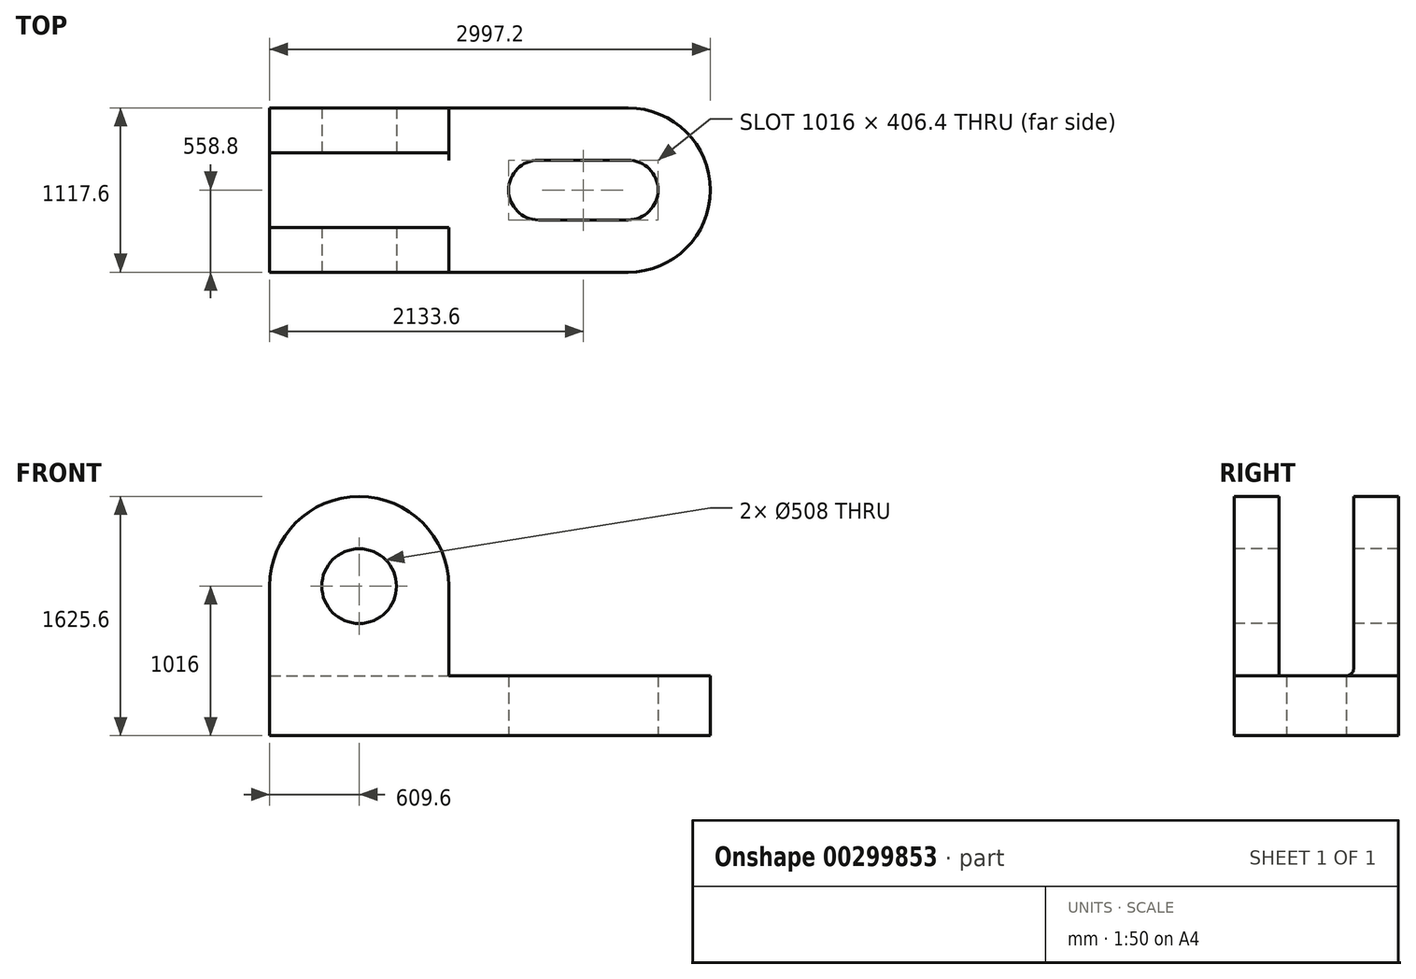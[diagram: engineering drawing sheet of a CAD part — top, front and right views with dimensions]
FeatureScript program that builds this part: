
annotation { "Feature Type Name" : "Feature", "Feature Type Description" : "" }
export const myFeature = defineFeature(function(context is Context, id is Id, definition is map)
    precondition{}
    {
        {
            var Q0;
            Q0=qCreatedBy(makeId("Top.planeOp"),FACE);
            var sketch = newSketch(context, id + "F0", { "sketchPlane" : qUnion([Q0])});
            skLineSegment(sketch, "E0", {"start": v(0, -558.8) * mm, "end": v(2438.4, -558.8) * mm});
            skArc(sketch, "E1", {"start": v(2438.4, -558.8) * mm, "mid": v(2997.2, 0) * mm, "end": v(2438.4, 558.8) * mm});
            skLineSegment(sketch, "E2", {"start": v(0, -558.8) * mm, "end": v(0, 558.8) * mm});
            skLineSegment(sketch, "E3", {"start": v(0, 558.8) * mm, "end": v(2438.4, 558.8) * mm});
            skArc(sketch, "E4", {"start": v(2438.4, 203.2) * mm, "mid": v(2641.6, 0) * mm, "end": v(2438.4, -203.2) * mm});
            skLineSegment(sketch, "E5", {"start": v(2438.4, 203.2) * mm, "end": v(1828.8, 203.2) * mm});
            skArc(sketch, "E6", {"start": v(1828.8, 203.2) * mm, "mid": v(1625.6, 0) * mm, "end": v(1828.8, -203.2) * mm});
            skLineSegment(sketch, "E7", {"start": v(1828.8, -203.2) * mm, "end": v(2438.4, -203.2) * mm});
            skSolve(sketch);
        }
        {
            var Q0;
            Q0 = qSketchRegion(id + "F0", true);
            extrude(context, id + "F1", {"entities" : qUnion([Q0]), "depth" : 406.4 * mm});
        }
        {
            var Q0;
            Q0=makeQuery(id+"F1.opExtrude","SWEPT_FACE",FACE,{"disambiguationData":[OSD([sQuery(id+"F0.wireOp",EDGE,"E0")])]});
            var sketch = newSketch(context, id + "F2", { "sketchPlane" : qUnion([Q0])});
            skPoint(sketch, "E8", {"position": v(609.6, 1016) * mm});
            skCircle(sketch, "E9", {"center": v(609.6, 1016) * mm, "radius": 254 * mm});
            skArc(sketch, "E10", {"start": v(0, 1016) * mm, "mid": v(609.6, 1625.6) * mm, "end": v(1219.2, 1016) * mm});
            skLineSegment(sketch, "E11", {"start": v(0, 1016) * mm, "end": v(0, 406.4) * mm});
            skLineSegment(sketch, "E12", {"start": v(1219.2, 1016) * mm, "end": v(1219.2, 406.4) * mm});
            skLineSegment(sketch, "E13", {"start": v(1219.2, 406.4) * mm, "end": v(0, 406.4) * mm});
            skSolve(sketch);
        }
        {
            var Q0;
            Q0 = qSketchRegion(id + "F2", true);
            extrude(context, id + "F3", {"entities" : qUnion([Q0]), "operationType" : NewBodyOperationType.ADD, "oppositeDirection" : true, "depth" : 1117.6 * mm});
        }
        {
            var Q0;
            Q0 = qSketchRegion(id + "F2", true);
            extrude(context, id + "F4", {"entities" : qUnion([Q0]), "operationType" : NewBodyOperationType.REMOVE, "oppositeDirection" : true, "depth" : 812.8 * mm});
        }
        {
            var Q0;
            Q0 = qSketchRegion(id + "F2", true);
            extrude(context, id + "F5", {"entities" : qUnion([Q0]), "operationType" : NewBodyOperationType.ADD, "oppositeDirection" : true, "depth" : 304.8 * mm});
        }
        {
            var Q0;
            Q0=makeQuery(id+"F5.opExtrude","SWEPT_EDGE",EDGE,{"disambiguationData":[OSD([sQuery(id+"F0.wireOp",EDGE,"E0"),sQuery(id+"F2.wireOp",EDGE,"E12"),sQuery(id+"F2.wireOp",EDGE,"E13")])]});
            var Q1;
            Q1=makeQuery(id+"F3.opExtrude","SWEPT_EDGE",EDGE,{"disambiguationData":[OSD([sQuery(id+"F0.wireOp",EDGE,"E0"),sQuery(id+"F2.wireOp",EDGE,"E12"),sQuery(id+"F2.wireOp",EDGE,"E13")])]});
            var Q2;
            Q2=makeQuery(id+"F5.opExtrude","CAP_EDGE",EDGE,{"disambiguationData":[OSD([sQuery(id+"F2.wireOp",EDGE,"E13")])],"isStart":false});
            var Q3;
            Q3=makeQuery(id+"F4.boolean.opBoolean","COPY",EDGE,{"derivedFrom":makeQuery(id+"F4.opExtrude","CAP_EDGE",EDGE,{"disambiguationData":[OSD([sQuery(id+"F2.wireOp",EDGE,"E13")])],"isStart":false})});
            fillet(context, id + "F6", {"entities" : qUnion([Q0, Q1, Q2, Q3]), "radius" : 50.8 * mm, "tangentPropagation" : true, "allowEdgeOverflow" : false});
        }
    });
